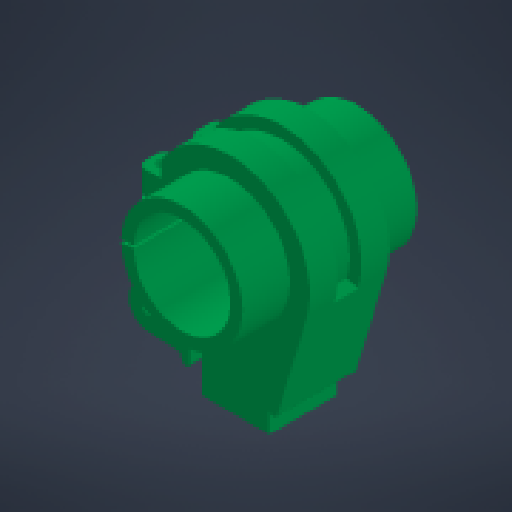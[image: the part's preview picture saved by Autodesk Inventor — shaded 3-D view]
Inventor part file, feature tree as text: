
AUTODESK INVENTOR PART (.ipt)
format: ipt  version: 2024 (Build 280153000, 153)  size: 526,336 bytes
history: native  units: mm
features: other x16, sketch x14, extrude x11, fillet x4, mirror x3, projected_geometry x2, reference x2, shell x1, sweep x1
ambient origin geometry x8: Origin, YZ Plane, XZ Plane, XY Plane, X Axis, Y Axis, Z Axis, Center Point
bodies: Body1 (feature_tree)
feature tree (54):
  other  "Твердое тело1"
  extrude  "Выдавливание1"  Depth=20.0mm
  shell  "Оболочка1"  Thickness=1.5mm
  extrude  "Выдавливание2"  Depth=20.0mm TaperAngle=0.0deg
  other  "РабПлоскость1"
  extrude  "Выдавливание4"  Depth=4.0mm
  sketch  "Эскиз8"
  other  "РабПлоскость3"
  sweep  "Сдвиг1"
  other  "РабОсь1"
  other  "РабПлоскость4"
  fillet  "Сопряжение2"  Radius=5.0mm
  other  "РабПлоскость5"
  other  "РабПлоскость6"
  other  "РабПлоскость7"
  other  "РабПлоскость8"
  extrude  "Выдавливание18"  Depth=20.0mm TaperAngle=0.0deg
  extrude  "Выдавливание19"  Depth=20.2mm
  extrude  "Выдавливание20"  Depth=24.4mm
  mirror  "Зеркальное отражение7"
  other  "Непосредственное редактирование3"
  fillet  "Сопряжение9"  Radius=8.0mm
  fillet  "Сопряжение10"  [1 undecoded]
  other  "Непосредственное редактирование4"
  extrude  "Выдавливание22"  Depth=3.0mm
  mirror  "Зеркальное отражение8"
  extrude  "Выдавливание23"  Depth=6.0mm
  extrude  "Выдавливание24"  Depth=1.0mm
  extrude  "Выдавливание25"  Depth=6.0mm
  mirror  "Зеркальное отражение9"
  extrude  "Выдавливание26"  Depth=16.25mm TaperAngle=0.0deg
  fillet  "Сопряжение11"  Radius=3.0mm
  sketch  "Эскиз1"
  sketch  "Эскиз2"
  projected_geometry  "Спроецированная петля1"
  sketch  "Эскиз5"
  reference  "Ссылка3"
  reference  "Ссылка4"
  sketch  "Эскиз10"
  sketch  "3D эскиз1"
  sketch  "Эскиз32"
  sketch  "Эскиз33"
  sketch  "Эскиз35"
  sketch  "Эскиз37"
  sketch  "Эскиз39"
  sketch  "Эскиз40"
  projected_geometry  "Спроецированная петля3"
  sketch  "Эскиз41"
  sketch  "Эскиз42"
  parser-record x1  (decoder bookkeeping rows leaked as tree rows — omitted from the tree; the rows remain in map.json)
  other  "arm_assembly.iam"
  other  "arm:1"
  other  "Перенос3"
  other  "Перенос4"
note: 1 required parameter value undecoded (feature->parameter linkage not recoverable at this tier; creation-order binding heuristic only, values carry confidence <= 0.55)
note: 1 file-system path scrubbed to <path> (originals preserved in map.json)
